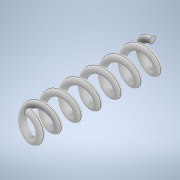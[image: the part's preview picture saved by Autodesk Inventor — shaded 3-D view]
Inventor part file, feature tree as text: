
AUTODESK INVENTOR PART (.ipt)
format: ipt  version: 2021 (Build 250183000, 183)  size: 436,224 bytes
history: native  units: in
note: dims shown in document units (in); Inventor stores cm internally (conversion verified against a paired STEP export)
features: helix x1, sketch x1
ambient origin geometry x8: Origin, YZ Plane, XZ Plane, XY Plane, X Axis, Y Axis, Z Axis, Center Point
bodies: Solid1 (feature_tree)
feature tree (2):
  helix  "Coil1"  [1 undecoded]
  sketch  "Sketch2"  dims[d1=0.0469in d2=1.0in d3=0.475in d4=2.3622in d5=0.0in d6=90.0deg d7=90.0deg d8=90.0deg d9=90.0deg]
note: 1 required parameter value undecoded (feature->parameter linkage not recoverable at this tier; creation-order binding heuristic only, values carry confidence <= 0.55)
